# Revit family: IS_ConnectSpace_E0371_BIM_DE
name_source: partatom
category: Plumbing Fixtures
revit_build: Autodesk Revit MEP 2016 (Build: 20161004_0715(x64)
units: mm (PartAtom-declared; Revit-internal decimal feet)

## family parameters
Always vertical = No
Cut with Voids When Loaded = No
Part Type = Normal
Room Calculation Point = No
Round Connector Dimension = Use Diameter
Shared = No
Work Plane-Based = No

## types (1)
- E0371 -  CONNECT SPACE vanity unit 436x243mm, 1 door
    Assembly Code = C1030200
    AssetType = Fest
    BIMobject category = Storage
    BOSUseNativeGeometries = 1
    Brand url = http://www.idealstandard.de
    Cost = 0 $
    CurrencyUnit = €
    CurrentRevision = 1
    Date of publishing = 15/09/2017
    Description = CONNECT SPACE vanity unit 436x243mm, 1 door
    DurationUnit = Jahr
    EAN code = https://5017830455042
    Edition number = 1
    IFC Classification = Sanitary Terminal
    Installation instructions = http://www.idealstandard.de
    Manufacturer name = Ideal Standard
    ManufacturerURL = http://www.idealstandard.de
    Model = E0371
    Nominal height = 520
    Nominal width = 436
    NominalDepth = 0 mm  [stored 0 ft]
    NominalHeight = 520 mm  [stored 1.70604 ft]
    NominalLength = 273 mm
    NominalWidth = 438 mm
    Product Guid = 0473cdfe-e93b-4117-9f61-bae591e89a6f
    Product SKU = E0371
    Product data url = https://bimobject.com
    Product family = CONNECT SPACE
    Product group = Furniture
    Product name = CONNECT SPACE vanity unit 436x243mm, 1 door
    Product url = http://www.idealstandard.de
    ProductInformation = www.idealstandard.de\produkte
    QR code = http://bimobject.com
    Size = 520x273x438 mm
    Space = Intern
    Technical description = http://www.idealstandard.de
    URL = http://www.idealstandard.de
    Uniclass 2.0 Code = Pr_40_30_78_03
    Uniclass 2.0 Description = Bathroom cabinets
    Uniclass 2015 Code = Pr_40_30_78_03
    Uniclass 2015 Name = Bathroom cabinets
    Uniclass2015Code = Pr_40_30_78_03
    Uniclass2015Title = Bathroom cabinets
    Uniclass2015Version = Products v1.1
    Version = 1
    VolumeUnits = Litres
    Weight Net (Kg) = 9.25

note: [stored X ft] marks values corroborated as IEEE doubles in the binary element streams (Revit-internal decimal feet)

## geometry (parser evidence)
native form markers: Blend x4, Sweep x1
no freeform markers — native parametric forms only
